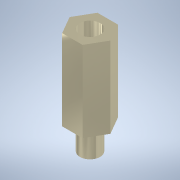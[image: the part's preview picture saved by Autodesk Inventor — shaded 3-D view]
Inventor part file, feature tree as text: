
AUTODESK INVENTOR PART (.ipt)
format: ipt  version: 2021 (Build 250183000, 183)  size: 110,592 bytes
history: native  units: mm
features: extrude x3, sketch x3
ambient origin geometry x8: Origin, YZ Plane, XZ Plane, XY Plane, X Axis, Y Axis, Z Axis, Center Point
bodies: Solid1 (feature_tree)
feature tree (6):
  extrude  "Extrusion1"  Depth=16.0mm TaperAngle=0.0deg
  extrude  "Extrusion2"  Depth=5.0mm TaperAngle=0.0deg
  extrude  "Extrusion3"  Depth=5.0mm TaperAngle=0.0deg
  sketch  "Sketch1"  dims[d0=7.0mm d1=16.0mm d2=0.0mm]
  sketch  "Sketch2"  dims[d3=4.0mm d4=5.0mm d5=0.0mm]
  sketch  "Sketch3"  dims[d6=4.0mm d7=5.0mm d8=0.0mm]
